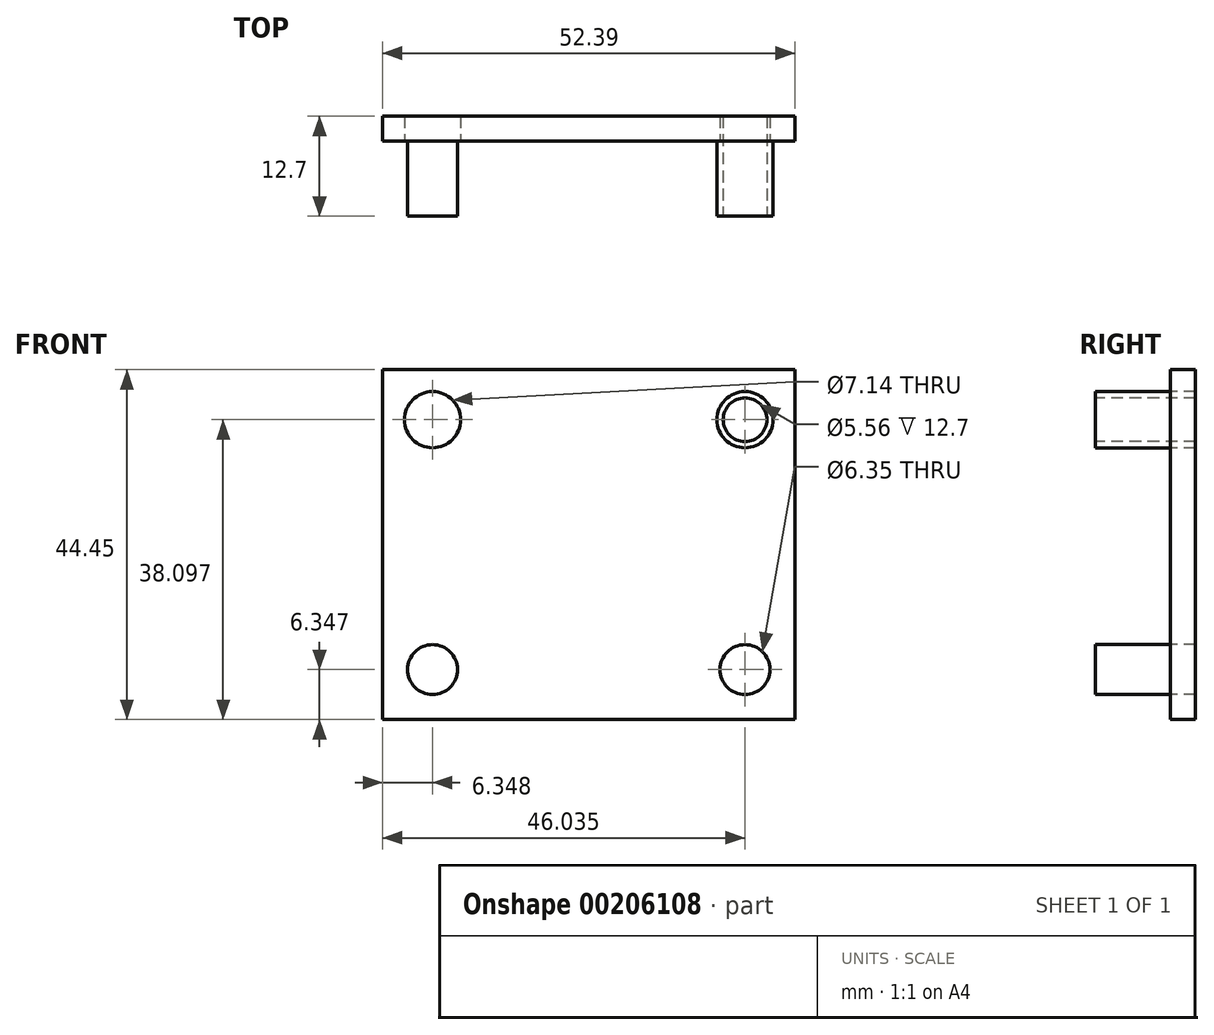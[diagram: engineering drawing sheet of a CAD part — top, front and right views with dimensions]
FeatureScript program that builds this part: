
annotation { "Feature Type Name" : "Feature", "Feature Type Description" : "" }
export const myFeature = defineFeature(function(context is Context, id is Id, definition is map)
    precondition{}
    {
        {
            var Q0;
            Q0=qCreatedBy(makeId("Front.planeOp"),FACE);
            var sketch = newSketch(context, id + "F0", { "sketchPlane" : qUnion([Q0])});
            skLineSegment(sketch, "E0.bottom", {"start": v(-24.21, 19.87) * mm, "end": v(28.18, 19.87) * mm});
            skLineSegment(sketch, "E0.top", {"start": v(-24.21, -24.58) * mm, "end": v(28.18, -24.58) * mm});
            skLineSegment(sketch, "E0.left", {"start": v(-24.21, 19.87) * mm, "end": v(-24.21, -24.58) * mm});
            skLineSegment(sketch, "E0.right", {"start": v(28.18, 19.87) * mm, "end": v(28.18, -24.58) * mm});
            skSolve(sketch);
        }
        {
            var Q0;
            Q0=makeQuery(id+"F0.imprint","IMPRINT",FACE,{"disambiguationData":[TD([[makeQuery(id+"F0.imprint","IMPRINT",EDGE,{"derivedFrom":sQuery(id+"F0.wireOp",EDGE,"E0.bottom")}),-1.0]])]});
            extrude(context, id + "F1", {"entities" : qUnion([Q0]), "depth" : 3.17 * mm});
        }
        {
            var Q0;
            Q0=makeQuery(id+"F1.opExtrude","CAP_FACE",FACE,{"disambiguationData":[OSD([sQuery(id+"F0.wireOp",EDGE,"E0.bottom"),sQuery(id+"F0.wireOp",EDGE,"E0.top"),sQuery(id+"F0.wireOp",EDGE,"E0.left"),sQuery(id+"F0.wireOp",EDGE,"E0.right")])],"isStart":false});
            var sketch = newSketch(context, id + "F2", { "sketchPlane" : qUnion([Q0])});
            skLineSegment(sketch, "E1", {"start": v(-24.21, 19.87) * mm, "end": v(-24.21, 13.52) * mm});
            skLineSegment(sketch, "E2", {"start": v(-24.21, 13.52) * mm, "end": v(-17.86, 13.52) * mm});
            skCircle(sketch, "E3", {"center": v(-17.86, 13.52) * mm, "radius": 3.57 * mm});
            skSolve(sketch);
        }
        {
            var Q0;
            Q0=makeQuery(id+"F2.imprint","IMPRINT",FACE,{"disambiguationData":[TD([[makeQuery(id+"F2.imprint","IMPRINT",EDGE,{"derivedFrom":sQuery(id+"F2.wireOp",EDGE,"E3")}),1.0]])]});
            extrude(context, id + "F3", {"entities" : qUnion([Q0]), "operationType" : NewBodyOperationType.REMOVE, "endBound" : BoundingType.THROUGH_ALL, "oppositeDirection" : true, "depth" : 25.4 * mm});
        }
        {
            var Q0;
            Q0=makeQuery(id+"F1.opExtrude","CAP_FACE",FACE,{"disambiguationData":[OSD([sQuery(id+"F0.wireOp",EDGE,"E0.bottom"),sQuery(id+"F0.wireOp",EDGE,"E0.top"),sQuery(id+"F0.wireOp",EDGE,"E0.left"),sQuery(id+"F0.wireOp",EDGE,"E0.right")])],"isStart":false});
            var sketch = newSketch(context, id + "F4", { "sketchPlane" : qUnion([Q0])});
            skLineSegment(sketch, "E4", {"start": v(28.18, 19.87) * mm, "end": v(28.18, 13.52) * mm});
            skLineSegment(sketch, "E5", {"start": v(28.18, 13.52) * mm, "end": v(21.83, 13.52) * mm});
            skCircle(sketch, "E6", {"center": v(21.83, 13.52) * mm, "radius": 3.57 * mm});
            skSolve(sketch);
        }
        {
            var Q0;
            Q0=makeQuery(id+"F4.imprint","IMPRINT",FACE,{"disambiguationData":[TD([[makeQuery(id+"F4.imprint","IMPRINT",EDGE,{"derivedFrom":sQuery(id+"F4.wireOp",EDGE,"E6")}),1.0]])]});
            extrude(context, id + "F5", {"entities" : qUnion([Q0]), "operationType" : NewBodyOperationType.ADD, "depth" : 9.52 * mm});
        }
        {
            var Q0;
            Q0=makeQuery(id+"F5.opExtrude","CAP_FACE",FACE,{"disambiguationData":[OSD([sQuery(id+"F4.wireOp",EDGE,"E6")])],"isStart":false});
            var sketch = newSketch(context, id + "F6", { "sketchPlane" : qUnion([Q0])});
            skCircle(sketch, "E7", {"center": v(21.83, 13.52) * mm, "radius": 2.78 * mm});
            skSolve(sketch);
        }
        {
            var Q0;
            Q0=makeQuery(id+"F6.imprint","IMPRINT",FACE,{"disambiguationData":[TD([[makeQuery(id+"F6.imprint","IMPRINT",EDGE,{"derivedFrom":sQuery(id+"F6.wireOp",EDGE,"E7")}),1.0]])]});
            extrude(context, id + "F7", {"entities" : qUnion([Q0]), "operationType" : NewBodyOperationType.REMOVE, "endBound" : BoundingType.THROUGH_ALL, "oppositeDirection" : true, "depth" : 25.4 * mm});
        }
        {
            var Q0;
            Q0=makeQuery(id+"F1.opExtrude","CAP_FACE",FACE,{"disambiguationData":[OSD([sQuery(id+"F0.wireOp",EDGE,"E0.bottom"),sQuery(id+"F0.wireOp",EDGE,"E0.top"),sQuery(id+"F0.wireOp",EDGE,"E0.left"),sQuery(id+"F0.wireOp",EDGE,"E0.right")])],"isStart":false});
            var sketch = newSketch(context, id + "F8", { "sketchPlane" : qUnion([Q0])});
            skLineSegment(sketch, "E8", {"start": v(-24.21, -24.58) * mm, "end": v(-24.21, -18.23) * mm});
            skLineSegment(sketch, "E9", {"start": v(-24.21, -18.23) * mm, "end": v(-17.86, -18.23) * mm});
            skCircle(sketch, "E10", {"center": v(-17.86, -18.23) * mm, "radius": 3.18 * mm});
            skSolve(sketch);
        }
        {
            var Q0;
            Q0=makeQuery(id+"F8.imprint","IMPRINT",FACE,{"disambiguationData":[TD([[makeQuery(id+"F8.imprint","IMPRINT",EDGE,{"derivedFrom":sQuery(id+"F8.wireOp",EDGE,"E10")}),1.0]])]});
            extrude(context, id + "F9", {"entities" : qUnion([Q0]), "operationType" : NewBodyOperationType.ADD, "depth" : 9.52 * mm});
        }
        {
            var Q0;
            Q0=makeQuery(id+"F1.opExtrude","CAP_FACE",FACE,{"disambiguationData":[OSD([sQuery(id+"F0.wireOp",EDGE,"E0.bottom"),sQuery(id+"F0.wireOp",EDGE,"E0.top"),sQuery(id+"F0.wireOp",EDGE,"E0.left"),sQuery(id+"F0.wireOp",EDGE,"E0.right")])],"isStart":false});
            var sketch = newSketch(context, id + "F10", { "sketchPlane" : qUnion([Q0])});
            skLineSegment(sketch, "E11", {"start": v(28.18, -24.58) * mm, "end": v(28.18, -18.23) * mm});
            skLineSegment(sketch, "E12", {"start": v(28.18, -18.23) * mm, "end": v(21.83, -18.23) * mm});
            skCircle(sketch, "E13", {"center": v(21.83, -18.23) * mm, "radius": 3.18 * mm});
            skSolve(sketch);
        }
        {
            var Q0;
            Q0=makeQuery(id+"F10.imprint","IMPRINT",FACE,{"disambiguationData":[TD([[makeQuery(id+"F10.imprint","IMPRINT",EDGE,{"derivedFrom":sQuery(id+"F10.wireOp",EDGE,"E13")}),1.0]])]});
            extrude(context, id + "F11", {"entities" : qUnion([Q0]), "operationType" : NewBodyOperationType.REMOVE, "endBound" : BoundingType.THROUGH_ALL, "oppositeDirection" : true, "depth" : 25.4 * mm});
        }
    });
